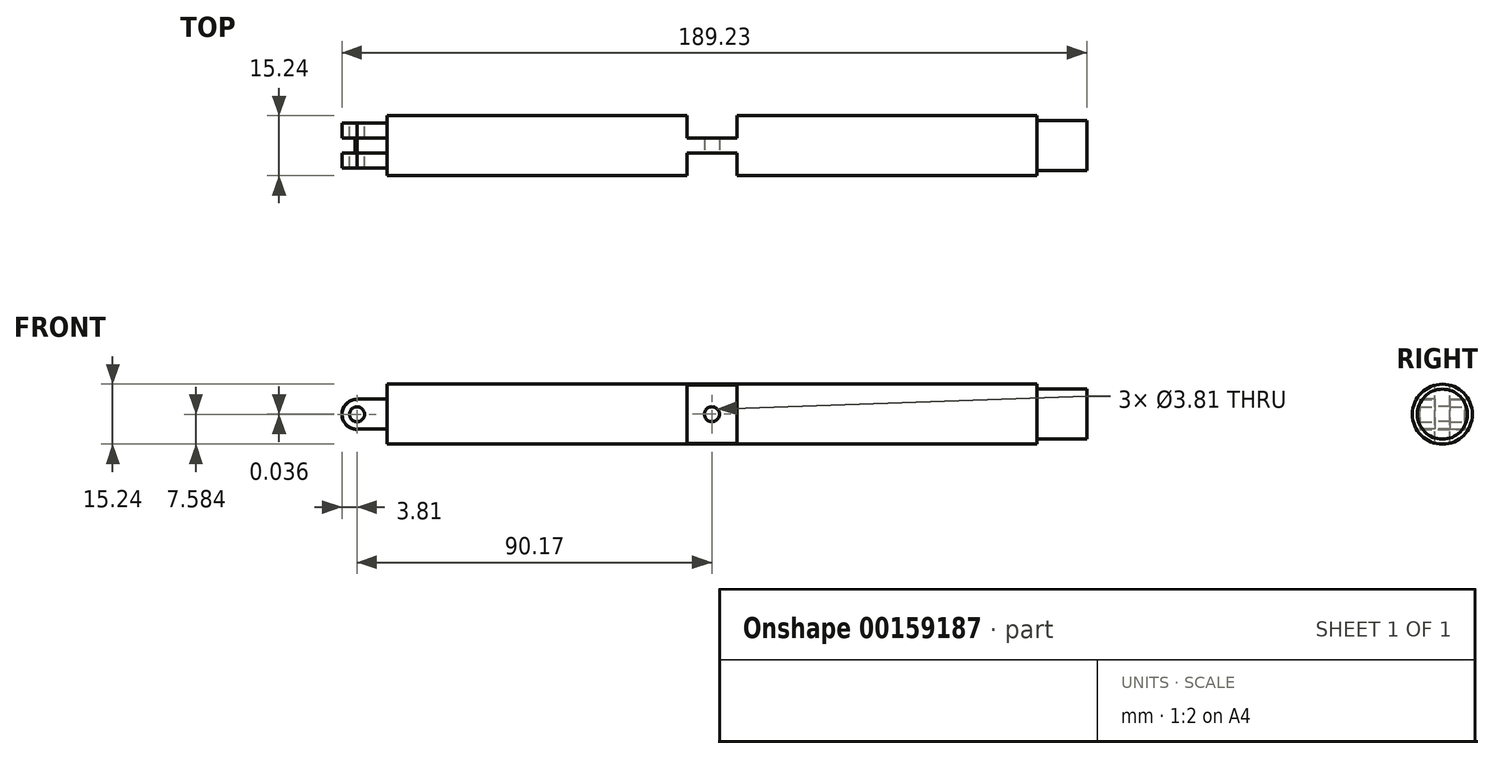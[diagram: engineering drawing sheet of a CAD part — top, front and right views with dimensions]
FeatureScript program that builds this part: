
annotation { "Feature Type Name" : "Feature", "Feature Type Description" : "" }
export const myFeature = defineFeature(function(context is Context, id is Id, definition is map)
    precondition{}
    {
        {
            var Q0;
            Q0=qCreatedBy(makeId("Right.planeOp"),FACE);
            var sketch = newSketch(context, id + "F0", { "sketchPlane" : qUnion([Q0])});
            skCircle(sketch, "E0", {"center": v(0, 0) * mm, "radius": 7.62 * mm});
            skSolve(sketch);
        }
        {
            var Q0;
            Q0=makeQuery(id+"F0.imprint","IMPRINT",FACE,{"disambiguationData":[TD([[makeQuery(id+"F0.imprint","IMPRINT",EDGE,{"derivedFrom":sQuery(id+"F0.wireOp",EDGE,"E0")}),1.0]])]});
            extrude(context, id + "F1", {"entities" : qUnion([Q0]), "depth" : 165.1 * mm});
        }
        {
            var Q0;
            Q0=makeQuery(id+"F1.opExtrude","CAP_FACE",FACE,{"disambiguationData":[OSD([sQuery(id+"F0.wireOp",EDGE,"E0")])],"isStart":false});
            var sketch = newSketch(context, id + "F2", { "sketchPlane" : qUnion([Q0])});
            skCircle(sketch, "E1", {"center": v(0, 0) * mm, "radius": 6.35 * mm});
            skSolve(sketch);
        }
        {
            var Q0;
            Q0=makeQuery(id+"F2.imprint","IMPRINT",FACE,{"disambiguationData":[TD([[makeQuery(id+"F2.imprint","IMPRINT",EDGE,{"derivedFrom":sQuery(id+"F2.wireOp",EDGE,"E1")}),1.0]])]});
            extrude(context, id + "F3", {"entities" : qUnion([Q0]), "operationType" : NewBodyOperationType.ADD, "depth" : 12.7 * mm});
        }
        {
            var Q0;
            Q0=makeQuery(id+"F1.opExtrude","CAP_FACE",FACE,{"disambiguationData":[OSD([sQuery(id+"F0.wireOp",EDGE,"E0")])],"isStart":true});
            var sketch = newSketch(context, id + "F4", { "sketchPlane" : qUnion([Q0])});
            skLineSegment(sketch, "E2.bottom", {"start": v(-1.9, 3.8) * mm, "end": v(1.9, 3.8) * mm});
            skLineSegment(sketch, "E2.top", {"start": v(-1.9, -3.81) * mm, "end": v(1.9, -3.81) * mm});
            skLineSegment(sketch, "E2.left", {"start": v(-1.9, 3.8) * mm, "end": v(-1.9, -3.81) * mm});
            skLineSegment(sketch, "E2.right", {"start": v(1.9, 3.8) * mm, "end": v(1.9, -3.81) * mm, "construction": true});
            skPoint(sketch, "E2.middle", {"position": v(0, 0) * mm});
            skLineSegment(sketch, "E3.bottom", {"start": v(-1.9, 3.8) * mm, "end": v(-5.72, 3.8) * mm});
            skLineSegment(sketch, "E3.top", {"start": v(-1.9, -3.8) * mm, "end": v(-5.71, -3.81) * mm});
            skLineSegment(sketch, "E3.left", {"start": v(-1.9, 3.8) * mm, "end": v(-1.9, -3.8) * mm});
            skLineSegment(sketch, "E3.right", {"start": v(-5.72, 3.8) * mm, "end": v(-5.71, -3.81) * mm});
            skLineSegment(sketch, "E4", {"start": v(0, 3.8) * mm, "end": v(0, 0) * mm, "construction": true});
            skLineSegment(sketch, "E5.MirrorCS", {"start": v(1.9, 3.8) * mm, "end": v(5.72, 3.8) * mm});
            skLineSegment(sketch, "E6.MirrorCS", {"start": v(1.9, 3.8) * mm, "end": v(1.9, -3.8) * mm});
            skLineSegment(sketch, "E7.MirrorCS", {"start": v(5.72, 3.8) * mm, "end": v(5.71, -3.81) * mm});
            skLineSegment(sketch, "E8.MirrorCS", {"start": v(1.9, -3.81) * mm, "end": v(5.71, -3.81) * mm});
            skSolve(sketch);
        }
        {
            var Q0;
            Q0=makeQuery(id+"F4.imprint","IMPRINT",FACE,{"disambiguationData":[TD([[makeQuery(id+"F4.imprint","IMPRINT",EDGE,{"derivedFrom":sQuery(id+"F4.wireOp",EDGE,"E3.bottom")}),1.0]])]});
            var Q1;
            Q1=makeQuery(id+"F4.imprint","IMPRINT",FACE,{"disambiguationData":[TD([[makeQuery(id+"F4.imprint","IMPRINT",EDGE,{"derivedFrom":sQuery(id+"F4.wireOp",EDGE,"E5.MirrorCS")}),-1.0]])]});
            extrude(context, id + "F5", {"entities" : qUnion([Q0, Q1]), "operationType" : NewBodyOperationType.ADD, "depth" : 7.62 * mm});
        }
        {
            var Q0;
            Q0=qCreatedBy(makeId("Front.planeOp"),FACE);
            var sketch = newSketch(context, id + "F6", { "sketchPlane" : qUnion([Q0])});
            skLineSegment(sketch, "E9", {"start": v(-7.62, 3.77) * mm, "end": v(-7.62, 1.87) * mm});
            skArc(sketch, "E10", {"start": v(-7.62, 3.77) * mm, "mid": v(-11.43, -0.04) * mm, "end": v(-7.62, -3.85) * mm});
            skCircle(sketch, "E11", {"center": v(-7.62, -0.04) * mm, "radius": 1.9 * mm});
            skLineSegment(sketch, "E12.trimOffspring", {"start": v(-7.62, -1.94) * mm, "end": v(-7.62, -3.85) * mm});
            skSolve(sketch);
        }
        {
            var Q0;
            {var subQ0=sQuery(id+"F6.wireOp",EDGE,"E9");Q0=makeQuery(id+"F6.imprint","IMPRINT",FACE,{"disambiguationData":[TD([[makeQuery(id+"F6.imprint","IMPRINT",EDGE,{"derivedFrom":subQ0}),-1.0]])]});}
            extrude(context, id + "F7", {"entities" : qUnion([Q0]), "operationType" : NewBodyOperationType.ADD, "endBound" : BoundingType.SYMMETRIC, "depth" : 11.43 * mm});
        }
        {
            var Q0;
            {var subQ0=sQuery(id+"F6.wireOp",EDGE,"E11");var subQ1=makeQuery(id+"F6.imprint","INTERSECT",VERTEX,{"derivedFrom":[sQuery(id+"F6.wireOp",EDGE,"E9"),subQ0]});Q0=makeQuery(id+"F6.imprint","IMPRINT",FACE,{"disambiguationData":[TD([[makeQuery(id+"F6.imprint","IMPRINT",EDGE,{"disambiguationData":[TD([[subQ1,-1.0]])],"derivedFrom":subQ0}),1.0]])]});}
            extrude(context, id + "F8", {"entities" : qUnion([Q0]), "operationType" : NewBodyOperationType.REMOVE, "endBound" : BoundingType.THROUGH_ALL, "oppositeDirection" : true, "depth" : 25.4 * mm});
        }
        {
            var Q0;
            {var subQ0=sQuery(id+"F6.wireOp",EDGE,"E11");var subQ1=makeQuery(id+"F6.imprint","INTERSECT",VERTEX,{"derivedFrom":[sQuery(id+"F6.wireOp",EDGE,"E9"),subQ0]});Q0=makeQuery(id+"F6.imprint","IMPRINT",FACE,{"disambiguationData":[TD([[makeQuery(id+"F6.imprint","IMPRINT",EDGE,{"disambiguationData":[TD([[subQ1,-1.0]])],"derivedFrom":subQ0}),1.0]])]});}
            extrude(context, id + "F9", {"entities" : qUnion([Q0]), "operationType" : NewBodyOperationType.REMOVE, "depth" : 25.4 * mm});
        }
        {
            var Q0;
            Q0=makeQuery(id+"F4.imprint","IMPRINT",FACE,{"disambiguationData":[TD([[makeQuery(id+"F4.imprint","IMPRINT",EDGE,{"derivedFrom":sQuery(id+"F4.wireOp",EDGE,"E2.bottom")}),-1.0]])]});
            extrude(context, id + "F10", {"entities" : qUnion([Q0]), "operationType" : NewBodyOperationType.REMOVE, "endBound" : BoundingType.THROUGH_ALL, "depth" : 25.4 * mm});
        }
        {
            var Q0;
            Q0=qCreatedBy(makeId("Top.planeOp"),FACE);
            var sketch = newSketch(context, id + "F11", { "sketchPlane" : qUnion([Q0])});
            skLineSegment(sketch, "E13.bottom", {"start": v(88.9, -7.65) * mm, "end": v(76.2, -7.65) * mm});
            skLineSegment(sketch, "E13.top", {"start": v(88.9, 7.65) * mm, "end": v(76.2, 7.65) * mm});
            skLineSegment(sketch, "E13.left", {"start": v(88.9, -7.65) * mm, "end": v(88.9, -1.9) * mm});
            skLineSegment(sketch, "E13.right", {"start": v(76.2, -7.65) * mm, "end": v(76.2, -1.9) * mm});
            skPoint(sketch, "E13.middle", {"position": v(82.55, 0) * mm});
            skLineSegment(sketch, "E14.bottom", {"start": v(76.2, 1.9) * mm, "end": v(88.9, 1.9) * mm});
            skLineSegment(sketch, "E14.top", {"start": v(76.2, -1.9) * mm, "end": v(88.9, -1.9) * mm});
            skLineSegment(sketch, "E15.trimOffspring", {"start": v(76.2, 1.9) * mm, "end": v(76.2, 7.65) * mm});
            skLineSegment(sketch, "E16.trimOffspring", {"start": v(88.9, 1.9) * mm, "end": v(88.9, 7.65) * mm});
            skSolve(sketch);
        }
        {
            var Q0;
            Q0 = qSketchRegion(id + "F11", true);
            extrude(context, id + "F12", {"entities" : qUnion([Q0]), "operationType" : NewBodyOperationType.REMOVE, "endBound" : BoundingType.THROUGH_ALL, "oppositeDirection" : true, "depth" : 25.4 * mm, "hasSecondDirection" : true, "secondDirectionOppositeDirection" : false, "secondDirectionDepth" : 25.4 * mm});
        }
        {
            var Q0;
            Q0=makeQuery(id+"F12.boolean.opBoolean","COPY",FACE,{"derivedFrom":makeQuery(id+"F12.opExtrude","SWEPT_FACE",FACE,{"disambiguationData":[OSD([sQuery(id+"F11.wireOp",EDGE,"E14.top")])]})});
            var sketch = newSketch(context, id + "F13", { "sketchPlane" : qUnion([Q0])});
            skCircle(sketch, "E17", {"center": v(82.55, 0) * mm, "radius": 1.9 * mm});
            skPoint(sketch, "E17.centerSnap0", {"position": v(82.55, 7.38) * mm});
            skSolve(sketch);
        }
        {
            var Q0;
            Q0=makeQuery(id+"F13.imprint","IMPRINT",FACE,{"disambiguationData":[TD([[makeQuery(id+"F13.imprint","IMPRINT",EDGE,{"derivedFrom":sQuery(id+"F13.wireOp",EDGE,"E17")}),1.0]])]});
            extrude(context, id + "F14", {"entities" : qUnion([Q0]), "operationType" : NewBodyOperationType.REMOVE, "endBound" : BoundingType.THROUGH_ALL, "oppositeDirection" : true, "depth" : 25.4 * mm});
        }
    });
